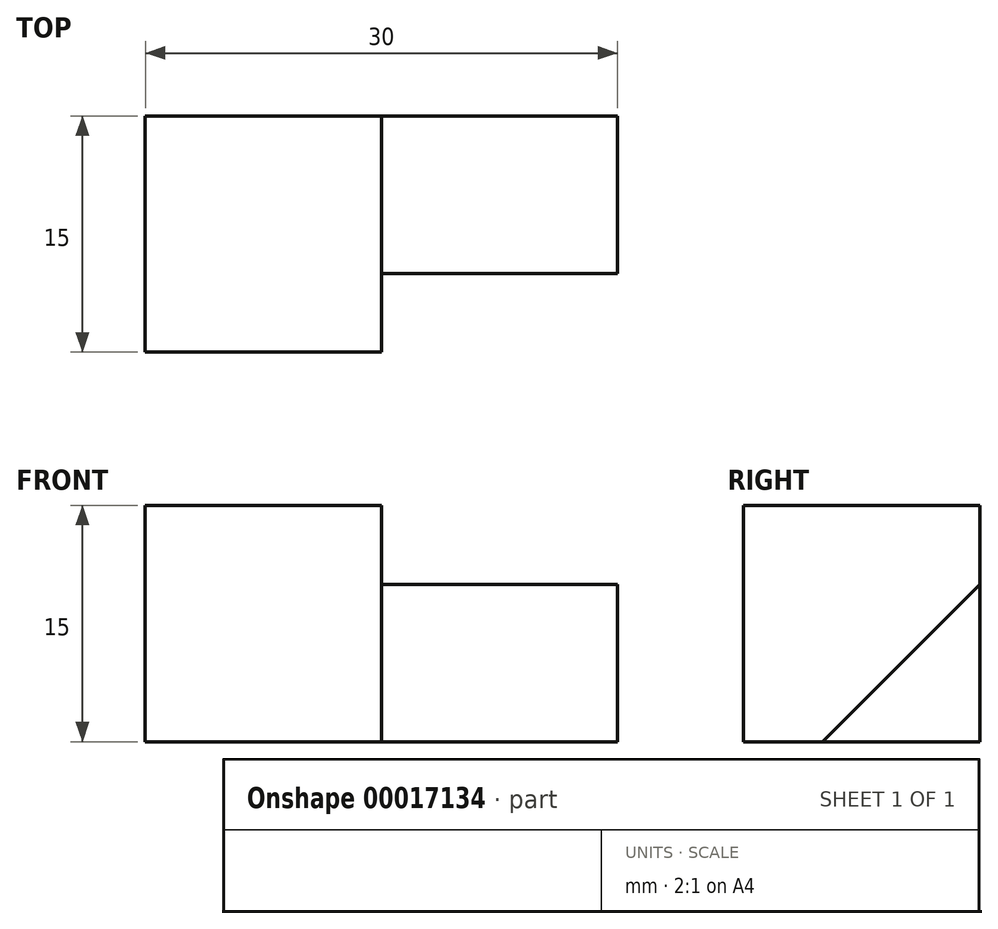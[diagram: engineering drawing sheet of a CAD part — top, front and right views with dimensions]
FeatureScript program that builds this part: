
annotation { "Feature Type Name" : "Feature", "Feature Type Description" : "" }
export const myFeature = defineFeature(function(context is Context, id is Id, definition is map)
    precondition{}
    {
        {
            var Q0;
            Q0=qCreatedBy(makeId("Front.planeOp"),FACE);
            var sketch = newSketch(context, id + "F0", { "sketchPlane" : qUnion([Q0])});
            skLineSegment(sketch, "E0.bottom", {"start": v(-11.93, 7.06) * mm, "end": v(3.07, 7.06) * mm});
            skLineSegment(sketch, "E0.top", {"start": v(-11.93, -7.94) * mm, "end": v(3.07, -7.94) * mm});
            skLineSegment(sketch, "E0.left", {"start": v(-11.93, 7.06) * mm, "end": v(-11.93, -7.94) * mm});
            skLineSegment(sketch, "E0.right", {"start": v(3.07, 7.06) * mm, "end": v(3.07, -7.94) * mm});
            skSolve(sketch);
        }
        {
            var Q0;
            Q0=makeQuery(id+"F0.imprint","IMPRINT",FACE,{"disambiguationData":[TD([[makeQuery(id+"F0.imprint","IMPRINT",EDGE,{"derivedFrom":sQuery(id+"F0.wireOp",EDGE,"E0.bottom")}),-1.0]])]});
            extrude(context, id + "F1", {"entities" : qUnion([Q0]), "depth" : 15 * mm});
        }
        {
            var Q0;
            Q0=makeQuery(id+"F1.opExtrude","SWEPT_FACE",FACE,{"disambiguationData":[OSD([sQuery(id+"F0.wireOp",EDGE,"E0.right")])]});
            var sketch = newSketch(context, id + "F2", { "sketchPlane" : qUnion([Q0])});
            skLineSegment(sketch, "E1", {"start": v(0, -7.94) * mm, "end": v(-10, -7.94) * mm});
            skLineSegment(sketch, "E2", {"start": v(0, -7.94) * mm, "end": v(0, 2.06) * mm});
            skLineSegment(sketch, "E3", {"start": v(-10, -7.94) * mm, "end": v(0, 2.06) * mm});
            skSolve(sketch);
        }
        {
            var Q0;
            Q0=makeQuery(id+"F2.imprint","IMPRINT",FACE,{"disambiguationData":[TD([[makeQuery(id+"F2.imprint","IMPRINT",EDGE,{"derivedFrom":sQuery(id+"F2.wireOp",EDGE,"E1")}),1.0]])]});
            extrude(context, id + "F3", {"entities" : qUnion([Q0]), "operationType" : NewBodyOperationType.ADD, "depth" : 15 * mm});
        }
    });
